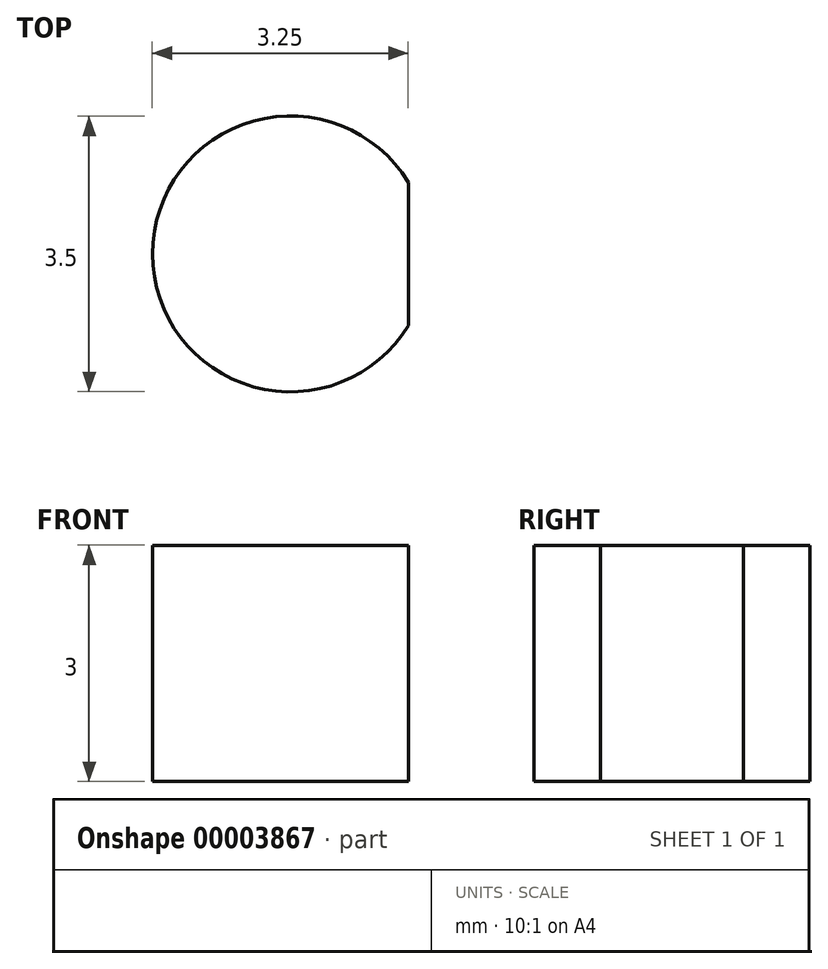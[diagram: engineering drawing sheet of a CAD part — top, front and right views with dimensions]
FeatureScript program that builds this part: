
annotation { "Feature Type Name" : "Feature", "Feature Type Description" : "" }
export const myFeature = defineFeature(function(context is Context, id is Id, definition is map)
    precondition{}
    {
        {
            var Q0;
            Q0=qCreatedBy(makeId("Top.planeOp"),FACE);
            var sketch = newSketch(context, id + "F0", { "sketchPlane" : qUnion([Q0])});
            skPoint(sketch, "E0.rect.middle", {"position": v(0, 0) * mm});
            skLineSegment(sketch, "E1", {"start": v(-25.58, 25.4) * mm, "end": v(25.58, 25.4) * mm});
            skLineSegment(sketch, "E2", {"start": v(25.58, 25.4) * mm, "end": v(25.58, 9.52) * mm});
            skLineSegment(sketch, "E3", {"start": v(25.58, 9.53) * mm, "end": v(28.58, 9.53) * mm});
            skLineSegment(sketch, "E4", {"start": v(28.57, 9.52) * mm, "end": v(28.58, 0) * mm});
            skLineSegment(sketch, "E5", {"start": v(-25.58, 25.4) * mm, "end": v(-25.58, 9.53) * mm});
            skLineSegment(sketch, "E6", {"start": v(-25.58, 9.53) * mm, "end": v(-28.58, 9.53) * mm});
            skLineSegment(sketch, "E7", {"start": v(-28.58, 9.53) * mm, "end": v(-28.58, 0) * mm});
            skLineSegment(sketch, "E8.0.MirrorCS", {"start": v(-28.58, -9.53) * mm, "end": v(-28.58, 0) * mm});
            skLineSegment(sketch, "E9.0.MirrorCS", {"start": v(-25.58, -9.53) * mm, "end": v(-28.58, -9.53) * mm});
            skLineSegment(sketch, "E10.0.MirrorCS", {"start": v(-25.58, -25.4) * mm, "end": v(-25.58, -9.53) * mm});
            skLineSegment(sketch, "E11.0.MirrorCS", {"start": v(-25.58, -25.4) * mm, "end": v(25.58, -25.4) * mm});
            skLineSegment(sketch, "E12.0.MirrorCS", {"start": v(25.58, -25.4) * mm, "end": v(25.58, -9.52) * mm});
            skLineSegment(sketch, "E13.0.MirrorCS", {"start": v(28.58, -9.52) * mm, "end": v(28.58, 0) * mm});
            skLineSegment(sketch, "E14.0.MirrorCS", {"start": v(25.58, -9.52) * mm, "end": v(28.58, -9.52) * mm});
            skSolve(sketch);
        }
        {
            var Q0;
            Q0 = qSketchRegion(id + "F0", true);
            extrude(context, id + "F1", {"entities" : qUnion([Q0]), "depth" : 3 * mm});
        }
        {
            var Q0;
            Q0=makeQuery(id+"F1.opExtrude","CAP_FACE",FACE,{"disambiguationData":[OSD([sQuery(id+"F0.wireOp",EDGE,"E1"),sQuery(id+"F0.wireOp",EDGE,"E2"),sQuery(id+"F0.wireOp",EDGE,"E3"),sQuery(id+"F0.wireOp",EDGE,"E5"),sQuery(id+"F0.wireOp",EDGE,"E6"),sQuery(id+"F0.wireOp",EDGE,"E7"),sQuery(id+"F0.wireOp",EDGE,"E9.0.MirrorCS"),sQuery(id+"F0.wireOp",EDGE,"E10.0.MirrorCS"),sQuery(id+"F0.wireOp",EDGE,"E11.0.MirrorCS"),sQuery(id+"F0.wireOp",EDGE,"E12.0.MirrorCS"),sQuery(id+"F0.wireOp",EDGE,"E13.0.MirrorCS"),sQuery(id+"F0.wireOp",EDGE,"E14.0.MirrorCS")])],"isStart":false});
            var sketch = newSketch(context, id + "F2", { "sketchPlane" : qUnion([Q0])});
            skCircle(sketch, "E15", {"center": v(-27.08, 0) * mm, "radius": 1.75 * mm});
            skCircle(sketch, "E16.0.MirrorC", {"center": v(27.08, 0) * mm, "radius": 1.75 * mm});
            skLineSegment(sketch, "E17.rect.bottom", {"start": v(6.35, -23.72) * mm, "end": v(-12.7, -23.72) * mm});
            skLineSegment(sketch, "E17.rect.top", {"start": v(6.35, -20.73) * mm, "end": v(-12.7, -20.73) * mm});
            skLineSegment(sketch, "E17.rect.left", {"start": v(6.35, -23.72) * mm, "end": v(6.35, -20.73) * mm});
            skLineSegment(sketch, "E17.rect.right", {"start": v(-12.7, -23.72) * mm, "end": v(-12.7, -20.73) * mm});
            skPoint(sketch, "E17.rect.middle", {"position": v(-3.17, -22.23) * mm});
            skSolve(sketch);
        }
        {
            var Q0;
            {var subQ0=makeQuery(id+"F1.opExtrude","CAP_EDGE",EDGE,{"disambiguationData":[OSD([sQuery(id+"F0.wireOp",EDGE,"E7")])],"isStart":false});var subQ1=sQuery(id+"F2.wireOp",EDGE,"E15");var subQ3=makeQuery(id+"F2.imprint","INTERSECT",VERTEX,{"disambiguationData":[OD(0.0)],"derivedFrom":[subQ0,subQ1]});var subQ5=makeQuery(id+"F1.opExtrude","CAP_EDGE",EDGE,{"disambiguationData":[OSD([sQuery(id+"F0.wireOp",EDGE,"E13.0.MirrorCS")])],"isStart":false});var subQ6=sQuery(id+"F2.wireOp",EDGE,"E16.0.MirrorC");var subQ8=makeQuery(id+"F2.imprint","INTERSECT",VERTEX,{"disambiguationData":[OD(0.0)],"derivedFrom":[subQ5,subQ6]});Q0=qUnion([makeQuery(id+"F2.imprint","IMPRINT",FACE,{"disambiguationData":[TD([[makeQuery(id+"F2.imprint","IMPRINT",EDGE,{"derivedFrom":sQuery(id+"F2.wireOp",EDGE,"E17.rect.bottom")}),-1.0]])]}),makeQuery(id+"F2.imprint","IMPRINT",FACE,{"disambiguationData":[TD([[makeQuery(id+"F2.imprint","IMPRINT",EDGE,{"disambiguationData":[TD([[subQ3,-1.0]])],"derivedFrom":subQ1}),1.0]])]}),makeQuery(id+"F2.imprint","IMPRINT",FACE,{"disambiguationData":[TD([[makeQuery(id+"F2.imprint","IMPRINT",EDGE,{"disambiguationData":[TD([[subQ8,-1.0]])],"derivedFrom":subQ6}),-1.0]])]}),makeQuery(id+"F2.imprint","IMPRINT",FACE,{"disambiguationData":[TD([[makeQuery(id+"F2.imprint","IMPRINT",EDGE,{"disambiguationData":[TD([[subQ3,1.0]])],"derivedFrom":subQ1}),1.0]])]}),makeQuery(id+"F2.imprint","IMPRINT",FACE,{"disambiguationData":[TD([[makeQuery(id+"F2.imprint","IMPRINT",EDGE,{"disambiguationData":[TD([[subQ8,1.0]])],"derivedFrom":subQ6}),-1.0]])]})]);}
            extrude(context, id + "F3", {"entities" : qUnion([Q0]), "operationType" : NewBodyOperationType.REMOVE, "oppositeDirection" : true, "depth" : 25.4 * mm});
        }
    });
